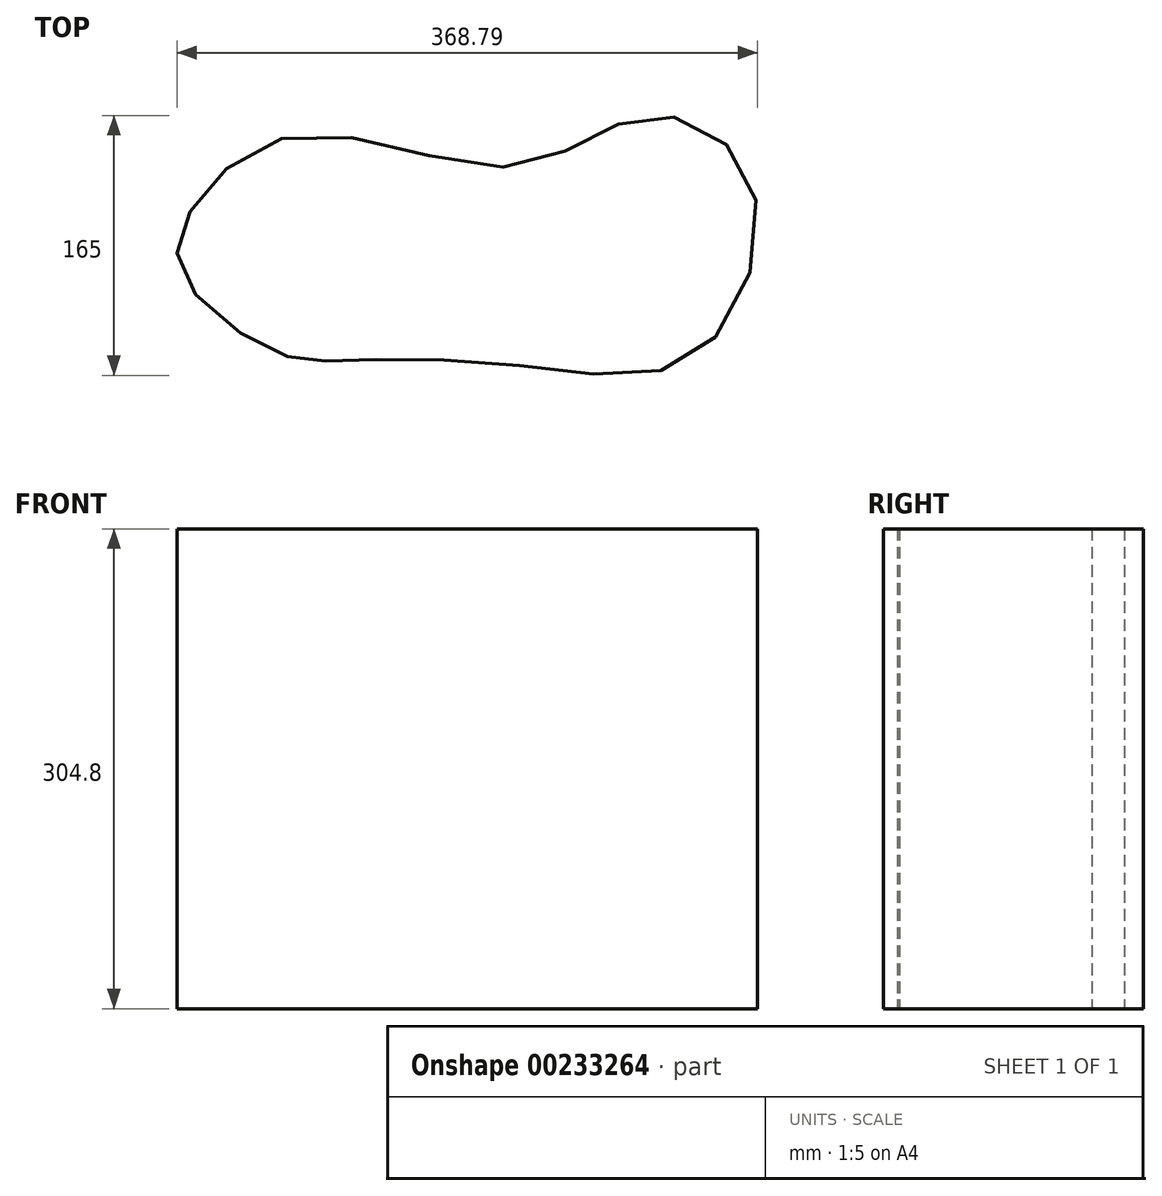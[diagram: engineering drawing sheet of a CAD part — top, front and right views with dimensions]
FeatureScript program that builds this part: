
annotation { "Feature Type Name" : "Feature", "Feature Type Description" : "" }
export const myFeature = defineFeature(function(context is Context, id is Id, definition is map)
    precondition{}
    {
        {
            var Q0;
            Q0=qCreatedBy(makeId("Top.planeOp"),FACE);
            var sketch = newSketch(context, id + "F0", { "sketchPlane" : qUnion([Q0])});
            skFitSpline(sketch, "E0", {"points": [v(-207.57, 19.5) * mm, v(-137.33, 68.2) * mm, v(0.33, 48.53) * mm, v(83.68, 80.37) * mm, v(149.23, 37.3) * mm, v(113.64, -71.34) * mm, v(-0.6, -77.9) * mm, v(-112.05, -75.08) * mm, v(-151.38, -70.4) * mm, v(-211.31, -22.64) * mm, v(-207.57, 19.5) * mm]});
            skSolve(sketch);
        }
        {
            var Q0;
            Q0 = qSketchRegion(id + "F0", true);
            extrude(context, id + "F1", {"entities" : qUnion([Q0]), "depth" : 304.8 * mm});
        }
    });
